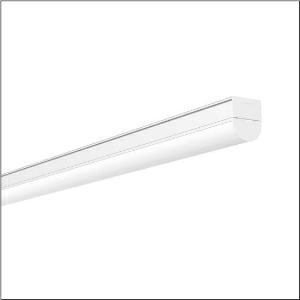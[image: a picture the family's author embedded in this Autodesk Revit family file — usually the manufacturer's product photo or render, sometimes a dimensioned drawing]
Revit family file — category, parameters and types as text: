
# Revit family: ecopack_r__31_51lj12mdm20a_29c1
name_source: partatom
category: Lighting Fixtures
units: mm (PartAtom-declared; Revit-internal decimal feet)

## family parameters
Cut with Voids When Loaded = No
Host = Face
Light Source = No
Part Type = Normal
Room Calculation Point = No
Round Connector Dimension = Use Diameter
Shared = No

## types (1)
- --- (1 x LED, 2510 lm, 20 W, 5000K)
    Apparent Load = 20 VA
    CIE Flux Codes = 41 71 90 93 100
    Color Rendering = 80
    Color Temperature = 5000K
    Default Elevation = 1800 mm
    Description = Ecopack® 31, diffuser luminaire, primary optical cover: cover, of PC, frosted, light emission: direct distribution, primary light characteristic: symmetric, installation type: surface-mounted, LED, rated luminous flux: 2.600lm, luminous efficacy: 130lm/W, light colour: 830/840/850, colour temperature: 3000/4000/5000K, control gear: ECG, with terminal, 3-pole, mains connection: 220..240V, AC, 50/60Hz, rated input power: 20W, housing, of aluminium, traffic white (RAL 9016), length: 600mm, width: 56mm, height: 68mm, end cap, of PC, white, protection rating (complete): IP20, insulation class (complete): insulation class I (protective earthing), certification: CE, impact resistance: IK06, permissible operating ambient temperature: -20..+40°C, packaging unit: 1 piece
    Height = 68 mm
    Lamp = 1 x LED
    Lamp Light Flux = 2510 lm
    Lamp Power = 20 W
    Lamp count = 1
    Length = 600 mm
    Luminous efficacy = 126 lm/W
    Manufacturer = Siteco
    ModVariant = No
    Model = 51LJ12MDM20A
    Mounting Place = Ceiling
    Mounting Type = Surface mounted
    Number of Poles = 1
    OnlyDefault = Yes
    Power Factor = 1
    Product Name = Ecopack® 31
    Product group = diffuser luminaire
    ProductGroupID = 304
    Protection Class = Protection class I
    Protection Degree = IP 20
    RLX_Detail_Level = 1
    RLX_Emergency_Light_Flux = 0 lm
    RLX_Emergency_Type = 0
    RLX_Emergency_Type_DB = No
    RlxData = <blob elided: 25529 chars, md5=db894291>
    Socket = socket
    Standby Power = 0 W
    System Light Flux = 2510 lm
    System Power = 20 W
    Type Comments = individual setting: colour temperature 5000K, luminous flux: 100 % | (ON | ON)
    Type Image = l_1007030.jpg
    URL = http://relux.com
    VarID = @adj_124983
    Voltage = 0 V
    Weight = 0.00 kg
    Width = 56 mm

## geometry (parser evidence)
native form markers: Blend x4, Sweep x13
no freeform markers — native parametric forms only
